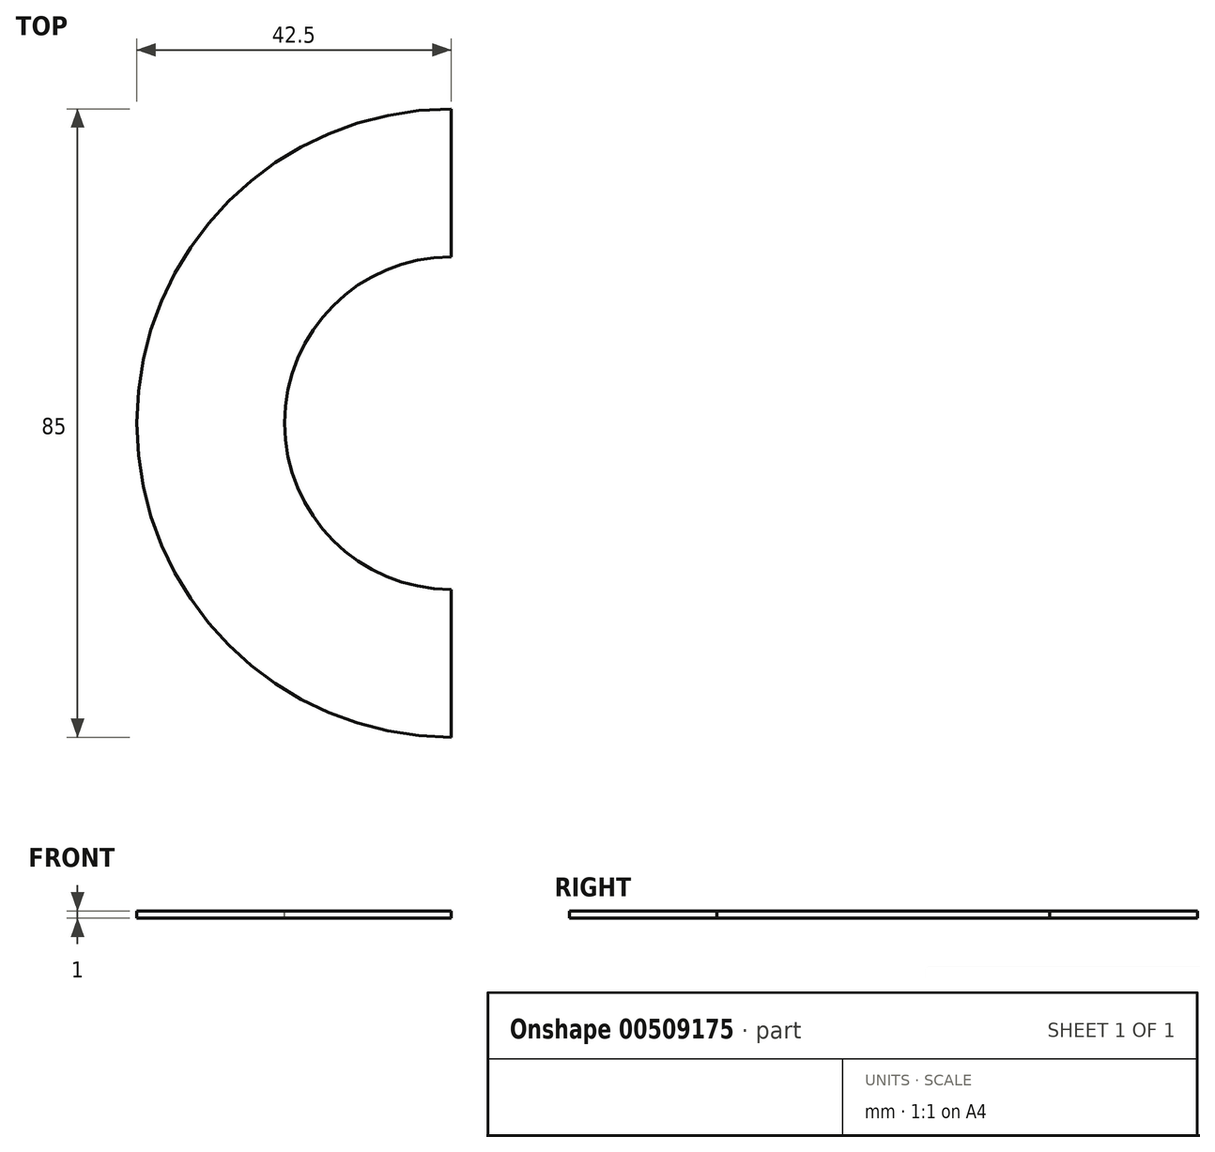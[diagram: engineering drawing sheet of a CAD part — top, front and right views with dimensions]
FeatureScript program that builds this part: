
annotation { "Feature Type Name" : "Feature", "Feature Type Description" : "" }
export const myFeature = defineFeature(function(context is Context, id is Id, definition is map)
    precondition{}
    {
        {
            var Q0;
            Q0=qCreatedBy(makeId("Top.planeOp"),FACE);
            var sketch = newSketch(context, id + "F0", { "sketchPlane" : qUnion([Q0])});
            skArc(sketch, "E0", {"start": v(0, 42.5) * mm, "mid": v(-42.5, 0) * mm, "end": v(0, -42.5) * mm});
            skArc(sketch, "E1", {"start": v(0, 22.5) * mm, "mid": v(-22.5, 0) * mm, "end": v(0, -22.5) * mm});
            skLineSegment(sketch, "E2", {"start": v(0, -42.5) * mm, "end": v(0, -22.5) * mm});
            skLineSegment(sketch, "E3.trimOffspring", {"start": v(0, 22.5) * mm, "end": v(0, 42.5) * mm});
            skSolve(sketch);
        }
        {
            var Q0;
            Q0=makeQuery(id+"F0.imprint","IMPRINT",FACE,{"disambiguationData":[TD([[makeQuery(id+"F0.imprint","IMPRINT",EDGE,{"derivedFrom":sQuery(id+"F0.wireOp",EDGE,"E0")}),1.0]])]});
            extrude(context, id + "F1", {"entities" : qUnion([Q0]), "oppositeDirection" : true, "depth" : 1 * mm});
        }
    });
